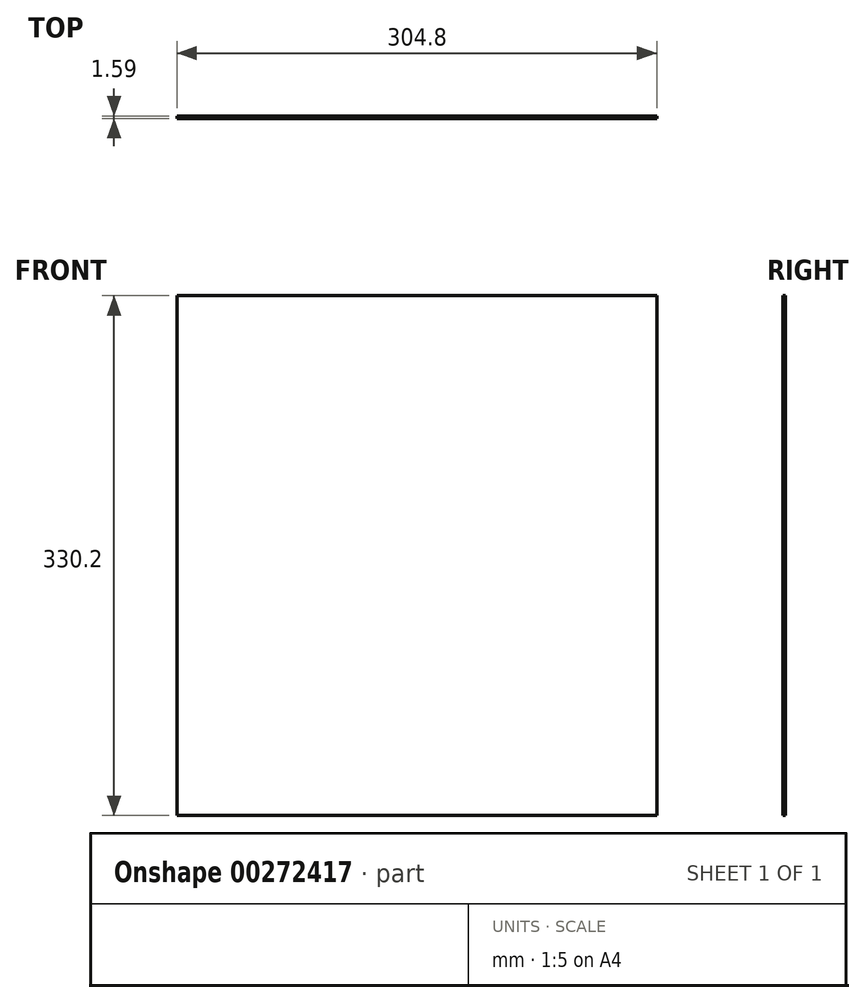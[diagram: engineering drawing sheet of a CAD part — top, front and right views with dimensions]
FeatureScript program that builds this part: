
annotation { "Feature Type Name" : "Feature", "Feature Type Description" : "" }
export const myFeature = defineFeature(function(context is Context, id is Id, definition is map)
    precondition{}
    {
        {
            var Q0;
            Q0=qCreatedBy(makeId("Front.planeOp"),FACE);
            var sketch = newSketch(context, id + "F0", { "sketchPlane" : qUnion([Q0])});
            skLineSegment(sketch, "E0.bottom", {"start": v(152.4, -165.1) * mm, "end": v(-152.4, -165.1) * mm});
            skLineSegment(sketch, "E0.top", {"start": v(152.4, 165.1) * mm, "end": v(-152.4, 165.1) * mm});
            skLineSegment(sketch, "E0.left", {"start": v(152.4, -165.1) * mm, "end": v(152.4, 165.1) * mm});
            skLineSegment(sketch, "E0.right", {"start": v(-152.4, -165.1) * mm, "end": v(-152.4, 165.1) * mm});
            skPoint(sketch, "E0.middle", {"position": v(0, 0) * mm});
            skSolve(sketch);
        }
        {
            var Q0;
            Q0=makeQuery(id+"F0.imprint","IMPRINT",FACE,{"disambiguationData":[TD([[makeQuery(id+"F0.imprint","IMPRINT",EDGE,{"derivedFrom":sQuery(id+"F0.wireOp",EDGE,"E0.bottom")}),-1.0]])]});
            extrude(context, id + "F1", {"entities" : qUnion([Q0]), "depth" : 1.59 * mm});
        }
    });
